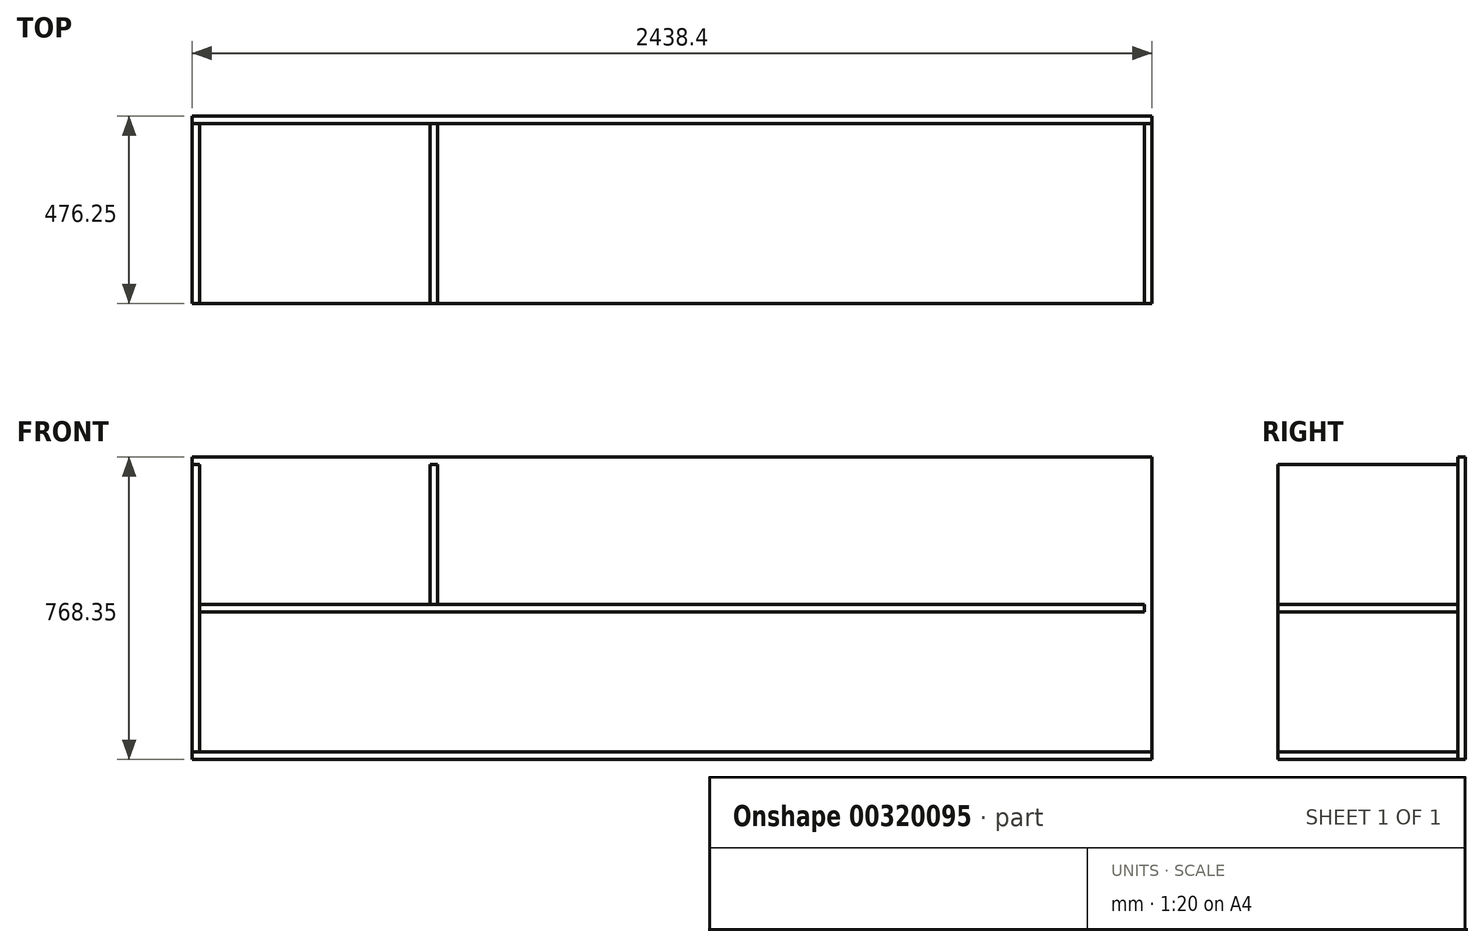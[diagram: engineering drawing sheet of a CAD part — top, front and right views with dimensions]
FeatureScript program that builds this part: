
annotation { "Feature Type Name" : "Feature", "Feature Type Description" : "" }
export const myFeature = defineFeature(function(context is Context, id is Id, definition is map)
    precondition{}
    {
        {
            var Q0;
            Q0=qCreatedBy(makeId("Front.planeOp"),FACE);
            var sketch = newSketch(context, id + "F0", { "sketchPlane" : qUnion([Q0])});
            skLineSegment(sketch, "E0.bottom", {"start": v(0, 0) * mm, "end": v(2438.4, 0) * mm});
            skLineSegment(sketch, "E0.top", {"start": v(0, -768.35) * mm, "end": v(2438.4, -768.35) * mm});
            skLineSegment(sketch, "E0.left", {"start": v(0, 0) * mm, "end": v(0, -768.35) * mm});
            skLineSegment(sketch, "E0.right", {"start": v(2438.4, 0) * mm, "end": v(2438.4, -768.35) * mm});
            skLineSegment(sketch, "E1", {"start": v(0, -19.05) * mm, "end": v(2438.4, -19.05) * mm});
            skLineSegment(sketch, "E2", {"start": v(0, -749.3) * mm, "end": v(2438.4, -749.3) * mm});
            skLineSegment(sketch, "E3", {"start": v(19.05, -19.05) * mm, "end": v(19.05, -749.3) * mm});
            skLineSegment(sketch, "E4", {"start": v(2419.35, -19.05) * mm, "end": v(2419.35, -749.3) * mm});
            skLineSegment(sketch, "E5", {"start": v(2419.35, -374.65) * mm, "end": v(19.05, -374.65) * mm});
            skLineSegment(sketch, "E6", {"start": v(2419.35, -393.7) * mm, "end": v(19.05, -393.7) * mm});
            skPoint(sketch, "E6.endSnap0", {"position": v(19.05, -384.18) * mm});
            skLineSegment(sketch, "E7", {"start": v(806.45, -393.7) * mm, "end": v(806.45, -749.3) * mm});
            skLineSegment(sketch, "E8", {"start": v(825.5, -393.7) * mm, "end": v(825.5, -749.3) * mm});
            skLineSegment(sketch, "E9", {"start": v(1612.9, -393.7) * mm, "end": v(1612.9, -749.3) * mm});
            skLineSegment(sketch, "E10", {"start": v(1631.95, -393.7) * mm, "end": v(1631.95, -749.3) * mm});
            skLineSegment(sketch, "E11", {"start": v(604.84, -19.05) * mm, "end": v(604.84, -374.65) * mm});
            skLineSegment(sketch, "E12", {"start": v(623.89, -19.05) * mm, "end": v(623.89, -374.65) * mm});
            skLineSegment(sketch, "E13", {"start": v(1209.67, -19.05) * mm, "end": v(1209.67, -374.65) * mm});
            skLineSegment(sketch, "E14", {"start": v(1228.73, -19.05) * mm, "end": v(1228.73, -374.65) * mm});
            skLineSegment(sketch, "E15", {"start": v(1814.51, -19.05) * mm, "end": v(1814.51, -374.65) * mm});
            skLineSegment(sketch, "E16", {"start": v(1833.56, -19.05) * mm, "end": v(1833.56, -374.65) * mm});
            skSolve(sketch);
        }
        {
            var Q0;
            {var subQ5=sQuery(id+"F0.wireOp",EDGE,"E0.top");Q0=makeQuery(id+"F0.imprint","IMPRINT",FACE,{"disambiguationData":[TD([[makeQuery(id+"F0.imprint","IMPRINT",EDGE,{"derivedFrom":subQ5}),1.0]])]});}
            extrude(context, id + "F1", {"entities" : qUnion([Q0]), "depth" : 457.2 * mm});
        }
        {
            var Q0;
            {var subQ1=sQuery(id+"F0.wireOp",EDGE,"E1");var subQ5=sQuery(id+"F0.wireOp",EDGE,"E0.left");var subQ8=makeQuery(id+"F0.imprint","INTERSECT",VERTEX,{"derivedFrom":[subQ5,subQ1]});Q0=makeQuery(id+"F0.imprint","IMPRINT",FACE,{"disambiguationData":[TD([[makeQuery(id+"F0.imprint","IMPRINT",EDGE,{"disambiguationData":[TD([[subQ8,-1.0]])],"derivedFrom":subQ5}),1.0]])]});}
            extrude(context, id + "F2", {"entities" : qUnion([Q0]), "depth" : 457.2 * mm});
        }
        {
            var Q0;
            {var subQ4=sQuery(id+"F0.wireOp",EDGE,"E5");var subQ10=sQuery(id+"F0.wireOp",EDGE,"E3");var subQ11=makeQuery(id+"F0.imprint","INTERSECT",VERTEX,{"derivedFrom":[subQ10,subQ4]});Q0=makeQuery(id+"F0.imprint","IMPRINT",FACE,{"disambiguationData":[TD([[makeQuery(id+"F0.imprint","IMPRINT",EDGE,{"disambiguationData":[TD([[subQ11,-1.0]])],"derivedFrom":subQ10}),1.0]])]});}
            extrude(context, id + "F3", {"entities" : qUnion([Q0]), "depth" : 457.2 * mm});
        }
        {
            var Q0;
            {var subQ0=sQuery(id+"F0.wireOp",EDGE,"E11");Q0=makeQuery(id+"F0.imprint","IMPRINT",FACE,{"disambiguationData":[TD([[makeQuery(id+"F0.imprint","IMPRINT",EDGE,{"derivedFrom":subQ0}),1.0]])]});}
            extrude(context, id + "F4", {"entities" : qUnion([Q0]), "depth" : 457.2 * mm});
        }
        {
            var Q0;
            {var subQ5=sQuery(id+"F0.wireOp",EDGE,"E0.top");Q0=makeQuery(id+"F0.imprint","IMPRINT",FACE,{"disambiguationData":[TD([[makeQuery(id+"F0.imprint","IMPRINT",EDGE,{"derivedFrom":subQ5}),1.0]])]});}
            var sketch = newSketch(context, id + "F5", { "sketchPlane" : qUnion([Q0])});
            skPoint(sketch, "E17.0", {"position": v(2438.4, -768.35) * mm});
            skLineSegment(sketch, "E18", {"start": v(2438.4, -768.35) * mm, "end": v(0, -768.35) * mm});
            skLineSegment(sketch, "E19", {"start": v(0, -768.35) * mm, "end": v(0, 0) * mm});
            skLineSegment(sketch, "E20", {"start": v(0, 0) * mm, "end": v(2438.4, 0) * mm});
            skLineSegment(sketch, "E21", {"start": v(2438.4, 0) * mm, "end": v(2438.4, -768.35) * mm});
            skSolve(sketch);
        }
        {
            var Q0;
            Q0 = qSketchRegion(id + "F5", true);
            extrude(context, id + "F6", {"entities" : qUnion([Q0]), "oppositeDirection" : true, "depth" : 19.05 * mm});
        }
    });
